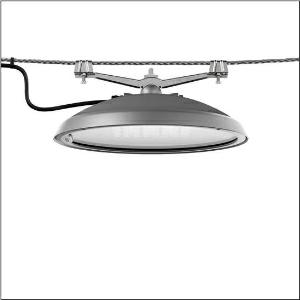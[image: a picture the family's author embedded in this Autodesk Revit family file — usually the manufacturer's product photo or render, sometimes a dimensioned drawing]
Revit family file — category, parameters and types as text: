
# Revit family: dl_r__50_iq_mini___st0_8s_5xa248v31f08ge_778c
name_source: partatom
category: Lighting Fixtures
units: mm (PartAtom-declared; Revit-internal decimal feet)

## family parameters
Cut with Voids When Loaded = No
Host = Face
Light Source = No
Part Type = Normal
Room Calculation Point = No
Round Connector Dimension = Use Diameter
Shared = No

## types (1)
- --- (1 x LED, 5190 lm, 32.7 W, 3000K)
    Apparent Load = 33 VA
    CIE Flux Codes = 38 75 97 100 100
    Color Rendering = 70
    Color Temperature = 3000K
    Default Elevation = 1800 mm
    Description = DL® 50 iQ mini, catenary luminaire, primary light control with lens, of PMMA, primary optical cover: cover, of toughened safety glass, transparent, light distribution: ST0.8s, light emission: direct distribution, primary light characteristic: symmetric, installation type: suspended mounting, LED, High Power LED, rated luminous flux: 5.190lm, luminous efficacy: 159lm/W, light colour: 730, colour temperature: 3000K, control: optimised constant luminous flux control (CLO 2.0), Desk-Remote (wireless, voltage-free reading and setting of iQ features in the workshop via application-optimized NFC function/RFID function), Light-Fading, Smart-Wire, Night-Set, Lumen-Switch, Temp-Guard, Auto-Match, Street-Remote, mains connection: 230..240V, AC, 50/60Hz, start of lifetime: 33W, end of service life: 34W, reduction: 16W, luminaire housing, of diecast aluminium, powder-coated, Siteco® metallic grey (DB 702S), diameter: 500mm, height: 115mm, protection rating (complete): IP66, insulation class (complete): insulation class II (safety insulation), certification: CE, ENEC, VDE, impact resistance: IK08, permissible operating ambient temperature for outdoor applications: -25..+40°C, standard-compliant lighting for roads and squares, packaging unit: 1 piece

Light Distribution: ST0.8s
    Height = 124 mm  [stored 0.406824 ft]
    Lamp = 1 x LED
    Lamp Light Flux = 5190 lm
    Lamp Power = 32.7 W
    Lamp count = 1
    Length = 500 mm
    Luminous efficacy = 159 lm/W
    Manufacturer = Siteco
    ModVariant = No
    Model = 5XA248V31F08GE
    Number of Poles = 1
    OnlyDefault = Yes
    Power Factor = 1
    Product Name = DL® 50 iQ mini | ST0.8s
    Product group = catenary luminaire
    ProductGroupID = 6300
    Protection Class = Protection class II
    Protection Degree = IP 66
    RLX_Detail_Level = 1
    RLX_Emergency_Light_Flux = 0 lm
    RLX_Emergency_Type = 0
    RLX_Emergency_Type_DB = No
    RlxData = <blob elided: 123465 chars, md5=b4ed3035>
    Socket = socket
    Standby Power = 0 W
    System Light Flux = 5190 lm
    System Power = 33 W
    Type Comments = factory setting: luminous flux: 100 % | dim-lin: 254 | 340 mA
    Type Image = l_1242791.jpg
    URL = http://relux.com
    VarID = @adj_072459
    Voltage = 0 V
    Weight = 0.00 kg
    Width = 0 mm  [stored 0 ft]

note: [stored X ft] marks values corroborated as IEEE doubles in the binary element streams (Revit-internal decimal feet)

## geometry (parser evidence)
native form markers: Blend x4, Sweep x13
no freeform markers — native parametric forms only
